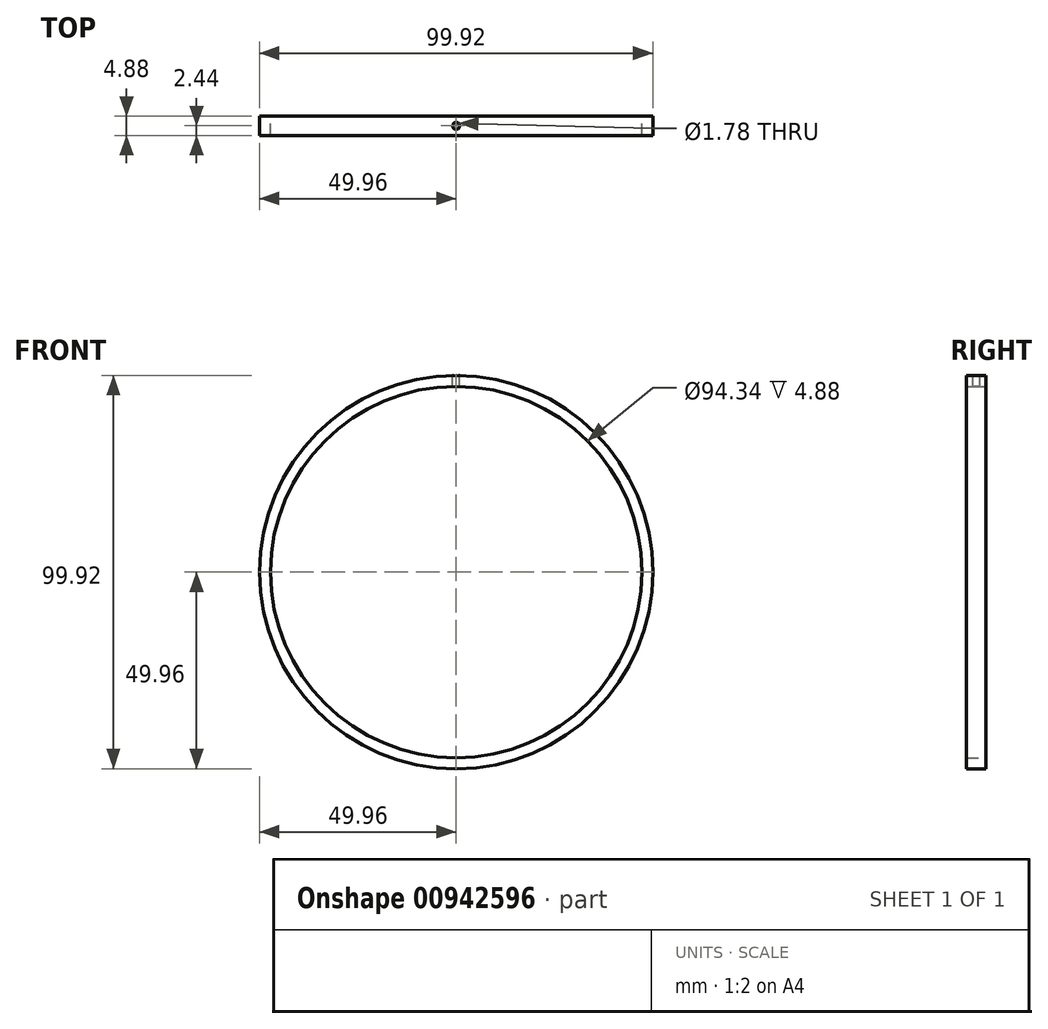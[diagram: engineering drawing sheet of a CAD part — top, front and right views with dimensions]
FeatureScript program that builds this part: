
annotation { "Feature Type Name" : "Feature", "Feature Type Description" : "" }
export const myFeature = defineFeature(function(context is Context, id is Id, definition is map)
    precondition{}
    {
        {
            var Q0;
            Q0=qCreatedBy(makeId("Front.planeOp"),FACE);
            var sketch = newSketch(context, id + "F0", { "sketchPlane" : qUnion([Q0])});
            skCircle(sketch, "E0", {"center": v(0, 0) * mm, "radius": 49.96 * mm});
            skCircle(sketch, "E1.0", {"center": v(0, 0) * mm, "radius": 47.17 * mm});
            skPoint(sketch, "E2", {"position": v(0, 49.96) * mm});
            skSolve(sketch);
        }
        {
            var Q0;
            Q0=makeQuery(id+"F0.imprint","IMPRINT",FACE,{"disambiguationData":[TD([[makeQuery(id+"F0.imprint","IMPRINT",EDGE,{"derivedFrom":sQuery(id+"F0.wireOp",EDGE,"E0")}),1.0]])]});
            extrude(context, id + "F1", {"entities" : qUnion([Q0]), "endBound" : BoundingType.SYMMETRIC, "depth" : 4.88 * mm, "offsetDistance" : 25.4 * mm});
        }
        {
            var Q0;
            Q0=sQuery(id+"F0.wireOp",VERTEX,"E2");
            var Q1;
            Q1=qCreatedBy(makeId("Top.planeOp"),FACE);
            cPlane(context, id + "F2", {"entities" : qUnion([Q0, Q1]), "cplaneType" : CPlaneType.PLANE_POINT, "offset" : 25.4 * mm, "width" : 152.4 * mm, "height" : 152.4 * mm});
        }
        {
            var Q0;
            Q0=qCreatedBy(id+"F2.planeOp",FACE);
            var sketch = newSketch(context, id + "F3", { "sketchPlane" : qUnion([Q0])});
            skCircle(sketch, "E3", {"center": v(0, 0) * mm, "radius": 3.7 * mm});
            skSolve(sketch);
        }
        {
            var Q0;
            Q0=sQuery(id+"F3.wireOp",VERTEX,"E3.center");
            var Q1;
            Q1=makeQuery(id+"F1.opExtrude","SWEPT_BODY",BODY,{"disambiguationData":[OSD([sQuery(id+"F0.wireOp",EDGE,"E0"),sQuery(id+"F0.wireOp",EDGE,"E1.0")])]});
            hole(context, id + "F4", {"style" : HoleStyle.SIMPLE, "endStyle" : HoleEndStyle.BLIND, "standardTappedOrClearance" : lookupTablePath({ "standard" : "ANSI", "engagement" : "75%", "pitch" : "56 tpi", "size" : "#2", "type" : "Tapped" }), "standardBlindInLast" : lookupTablePath({ "standard" : "ANSI", "fit" : "Normal", "engagement" : "75%", "pitch" : "56 tpi", "size" : "#2", "type" : "Clearance & tapped" }), "holeDiameter" : 1.78 * mm, "majorDiameter" : 2.18 * mm, "showTappedDepth" : true, "holeDepth" : 14.06 * mm, "isTappedThrough" : true, "tappedDepth" : 12.7 * mm, "tapClearance" : 3, "locations" : qUnion([Q0]), "scope" : qUnion([Q1])});
        }
    });
